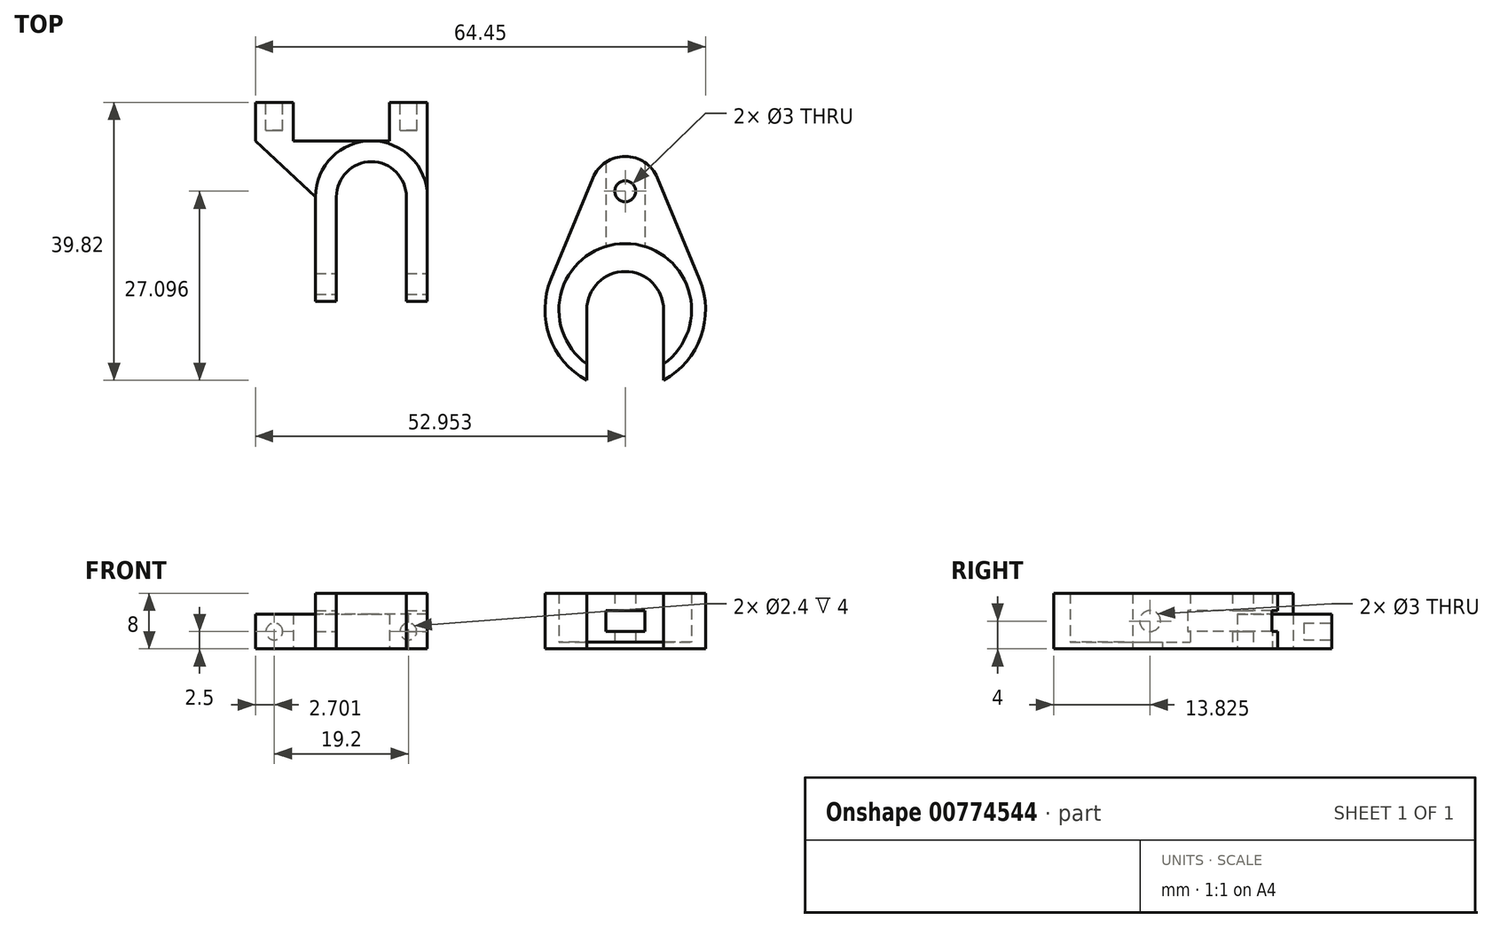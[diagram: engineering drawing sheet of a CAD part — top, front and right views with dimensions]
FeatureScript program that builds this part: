
annotation { "Feature Type Name" : "Feature", "Feature Type Description" : "" }
export const myFeature = defineFeature(function(context is Context, id is Id, definition is map)
    precondition{}
    {
        {
            var Q0;
            Q0=qCreatedBy(makeId("Top.planeOp"),FACE);
            var sketch = newSketch(context, id + "F0", { "sketchPlane" : qUnion([Q0])});
            skArc(sketch, "E0", {"start": v(-9.2, 19.48) * mm, "mid": v(-14.2, 24.48) * mm, "end": v(-19.2, 19.48) * mm});
            skArc(sketch, "E1.0", {"start": v(-6.2, 19.48) * mm, "mid": v(-14.2, 27.48) * mm, "end": v(-22.2, 19.48) * mm});
            skLineSegment(sketch, "E2", {"start": v(-22.2, 19.48) * mm, "end": v(-22.2, 4.48) * mm});
            skLineSegment(sketch, "E3", {"start": v(-22.2, 4.48) * mm, "end": v(-19.2, 4.48) * mm});
            skLineSegment(sketch, "E4", {"start": v(-19.2, 4.48) * mm, "end": v(-19.2, 19.48) * mm});
            skLineSegment(sketch, "E5", {"start": v(-9.2, 19.48) * mm, "end": v(-9.2, 4.48) * mm});
            skLineSegment(sketch, "E6", {"start": v(-9.2, 4.48) * mm, "end": v(-6.2, 4.48) * mm});
            skLineSegment(sketch, "E7", {"start": v(-6.2, 4.48) * mm, "end": v(-6.2, 19.48) * mm});
            skLineSegment(sketch, "E8", {"start": v(-8.9, 32.98) * mm, "end": v(-11.6, 32.98) * mm});
            skLineSegment(sketch, "E9", {"start": v(-25.4, 27.48) * mm, "end": v(-11.6, 27.48) * mm});
            skLineSegment(sketch, "E10", {"start": v(-11.6, 32.98) * mm, "end": v(-11.6, 27.48) * mm});
            skLineSegment(sketch, "E11", {"start": v(-28.1, 32.98) * mm, "end": v(-30.8, 32.98) * mm});
            skLineSegment(sketch, "E12", {"start": v(-30.8, 32.98) * mm, "end": v(-30.8, 27.48) * mm});
            skLineSegment(sketch, "E13", {"start": v(-30.8, 27.48) * mm, "end": v(-22.2, 19.48) * mm});
            skLineSegment(sketch, "E14", {"start": v(-28.1, 32.98) * mm, "end": v(-25.4, 32.98) * mm});
            skLineSegment(sketch, "E15", {"start": v(-25.4, 32.98) * mm, "end": v(-25.4, 27.48) * mm});
            skLineSegment(sketch, "E16.trimOffspring", {"start": v(-25.4, 32.98) * mm, "end": v(-28.1, 32.98) * mm});
            skLineSegment(sketch, "E17", {"start": v(-6.2, 19.48) * mm, "end": v(-6.2, 32.98) * mm});
            skLineSegment(sketch, "E18", {"start": v(-6.2, 32.98) * mm, "end": v(-8.9, 32.98) * mm});
            skSolve(sketch);
        }
        {
            var Q0;
            Q0=makeQuery(id+"F0.imprint","IMPRINT",FACE,{"disambiguationData":[TD([[makeQuery(id+"F0.imprint","IMPRINT",EDGE,{"derivedFrom":sQuery(id+"F0.wireOp",EDGE,"E0")}),-1.0]])]});
            extrude(context, id + "F1", {"entities" : qUnion([Q0]), "depth" : 8 * mm, "offsetDistance" : 25 * mm});
        }
        {
            var Q0;
            Q0=makeQuery(id+"F0.imprint","IMPRINT",FACE,{"disambiguationData":[TD([[makeQuery(id+"F0.imprint","IMPRINT",EDGE,{"derivedFrom":sQuery(id+"F0.wireOp",EDGE,"E9")}),-1.0]])]});
            var Q1;
            Q1=makeQuery(id+"F0.imprint","IMPRINT",FACE,{"disambiguationData":[TD([[makeQuery(id+"F0.imprint","IMPRINT",EDGE,{"derivedFrom":sQuery(id+"F0.wireOp",EDGE,"E11")}),1.0]])]});
            extrude(context, id + "F2", {"entities" : qUnion([Q0, Q1]), "operationType" : NewBodyOperationType.ADD, "depth" : 5 * mm, "offsetDistance" : 25 * mm});
        }
        {
            var Q0;
            Q0=makeQuery(id+"F2.opExtrude","SWEPT_FACE",FACE,{"disambiguationData":[OSD([sQuery(id+"F0.wireOp",EDGE,"E11"),sQuery(id+"F0.wireOp",EDGE,"E16.trimOffspring")])]});
            var sketch = newSketch(context, id + "F3", { "sketchPlane" : qUnion([Q0])});
            skLineSegment(sketch, "E19", {"start": v(25.4, 0) * mm, "end": v(30.8, 0) * mm});
            skCircle(sketch, "E20", {"center": v(28.1, 2.5) * mm, "radius": 1.2 * mm});
            skPoint(sketch, "E21.orphan", {"position": v(25.4, 5) * mm});
            skLineSegment(sketch, "E22", {"start": v(28.1, 2.5) * mm, "end": v(8.9, 2.5) * mm});
            skCircle(sketch, "E23", {"center": v(8.9, 2.5) * mm, "radius": 1.2 * mm});
            skSolve(sketch);
        }
        {
            var Q0;
            Q0=makeQuery(id+"F3.imprint","IMPRINT",FACE,{"disambiguationData":[TD([[makeQuery(id+"F3.imprint","IMPRINT",EDGE,{"derivedFrom":sQuery(id+"F3.wireOp",EDGE,"E23")}),1.0]])]});
            var Q1;
            Q1=makeQuery(id+"F3.imprint","IMPRINT",FACE,{"disambiguationData":[TD([[makeQuery(id+"F3.imprint","IMPRINT",EDGE,{"derivedFrom":sQuery(id+"F3.wireOp",EDGE,"E20")}),1.0]])]});
            extrude(context, id + "F4", {"entities" : qUnion([Q0, Q1]), "operationType" : NewBodyOperationType.REMOVE, "oppositeDirection" : true, "depth" : 4 * mm, "offsetDistance" : 25 * mm});
        }
        {
            var Q0;
            Q0=makeQuery(id+"F1.opExtrude","SWEPT_FACE",FACE,{"disambiguationData":[OSD([sQuery(id+"F0.wireOp",EDGE,"E7")])]});
            var sketch = newSketch(context, id + "F5", { "sketchPlane" : qUnion([Q0])});
            skLineSegment(sketch, "E24", {"start": v(6.98, 4) * mm, "end": v(6.98, 2.5) * mm});
            skCircle(sketch, "E25", {"center": v(6.98, 4) * mm, "radius": 1.5 * mm});
            skSolve(sketch);
        }
        {
            var Q0;
            Q0=makeQuery(id+"F5.imprint","IMPRINT",FACE,{"disambiguationData":[TD([[makeQuery(id+"F5.imprint","IMPRINT",EDGE,{"derivedFrom":sQuery(id+"F5.wireOp",EDGE,"E25")}),1.0]])]});
            extrude(context, id + "F6", {"entities" : qUnion([Q0]), "operationType" : NewBodyOperationType.REMOVE, "oppositeDirection" : true, "depth" : 20 * mm, "offsetDistance" : 25 * mm});
        }
        {
            var Q0;
            Q0=qCreatedBy(makeId("Top.planeOp"),FACE);
            var sketch = newSketch(context, id + "F7", { "sketchPlane" : qUnion([Q0])});
            skArc(sketch, "E26", {"start": v(27.65, -4.49) * mm, "mid": v(22.15, 12.76) * mm, "end": v(16.65, -4.49) * mm});
            skArc(sketch, "E27.0", {"start": v(27.65, -6.84) * mm, "mid": v(22.15, 14.76) * mm, "end": v(16.65, -6.84) * mm});
            skLineSegment(sketch, "E28.left", {"start": v(27.65, 3.26) * mm, "end": v(27.65, -6.84) * mm});
            skLineSegment(sketch, "E28.right", {"start": v(16.65, 3.26) * mm, "end": v(16.65, -6.84) * mm});
            skArc(sketch, "E29", {"start": v(27.65, 3.26) * mm, "mid": v(22.15, 8.76) * mm, "end": v(16.65, 3.26) * mm});
            skPoint(sketch, "E30", {"position": v(22.15, 20.26) * mm});
            skCircle(sketch, "E31", {"center": v(22.15, 20.26) * mm, "radius": 1.5 * mm});
            skArc(sketch, "E32", {"start": v(26.77, 22.17) * mm, "mid": v(22.15, 25.26) * mm, "end": v(17.53, 22.17) * mm});
            skLineSegment(sketch, "E33", {"start": v(17.53, 22.17) * mm, "end": v(11.52, 7.65) * mm});
            skLineSegment(sketch, "E34", {"start": v(26.77, 22.17) * mm, "end": v(32.78, 7.65) * mm});
            skSolve(sketch);
        }
        {
            var Q0;
            Q0=makeQuery(id+"F7.imprint","IMPRINT",FACE,{"disambiguationData":[TD([[makeQuery(id+"F7.imprint","IMPRINT",EDGE,{"derivedFrom":sQuery(id+"F7.wireOp",EDGE,"E31")}),-1.0]])]});
            var Q1;
            {var subQ7=sQuery(id+"F7.wireOp",EDGE,"E26");Q1=makeQuery(id+"F7.imprint","IMPRINT",FACE,{"disambiguationData":[TD([[makeQuery(id+"F7.imprint","IMPRINT",EDGE,{"derivedFrom":subQ7}),-1.0]])]});}
            extrude(context, id + "F8", {"entities" : qUnion([Q0, Q1]), "depth" : 8 * mm, "offsetDistance" : 25 * mm});
        }
        {
            var Q0;
            {var subQ0=sQuery(id+"F7.wireOp",EDGE,"E26");Q0=makeQuery(id+"F7.imprint","IMPRINT",FACE,{"disambiguationData":[TD([[makeQuery(id+"F7.imprint","IMPRINT",EDGE,{"derivedFrom":subQ0}),1.0]])]});}
            extrude(context, id + "F9", {"entities" : qUnion([Q0]), "operationType" : NewBodyOperationType.ADD, "depth" : 1 * mm, "offsetDistance" : 25 * mm});
        }
        {
            var Q0;
            Q0=qCreatedBy(makeId("Front.planeOp"),FACE);
            var sketch = newSketch(context, id + "F10", { "sketchPlane" : qUnion([Q0])});
            skLineSegment(sketch, "E35.bottom", {"start": v(24.95, 5.5) * mm, "end": v(19.35, 5.5) * mm});
            skLineSegment(sketch, "E35.top", {"start": v(24.95, 2.5) * mm, "end": v(19.35, 2.5) * mm});
            skLineSegment(sketch, "E35.left", {"start": v(24.95, 5.5) * mm, "end": v(24.95, 2.5) * mm});
            skLineSegment(sketch, "E35.right", {"start": v(19.35, 5.5) * mm, "end": v(19.35, 2.5) * mm});
            skPoint(sketch, "E35.middle", {"position": v(22.15, 4) * mm});
            skSolve(sketch);
        }
        {
            var Q0;
            Q0=makeQuery(id+"F10.imprint","IMPRINT",FACE,{"disambiguationData":[TD([[makeQuery(id+"F10.imprint","IMPRINT",EDGE,{"derivedFrom":sQuery(id+"F10.wireOp",EDGE,"E35.bottom")}),1.0]])]});
            extrude(context, id + "F11", {"entities" : qUnion([Q0]), "operationType" : NewBodyOperationType.REMOVE, "oppositeDirection" : true, "depth" : 31.2 * mm, "offsetDistance" : 25 * mm});
        }
    });
